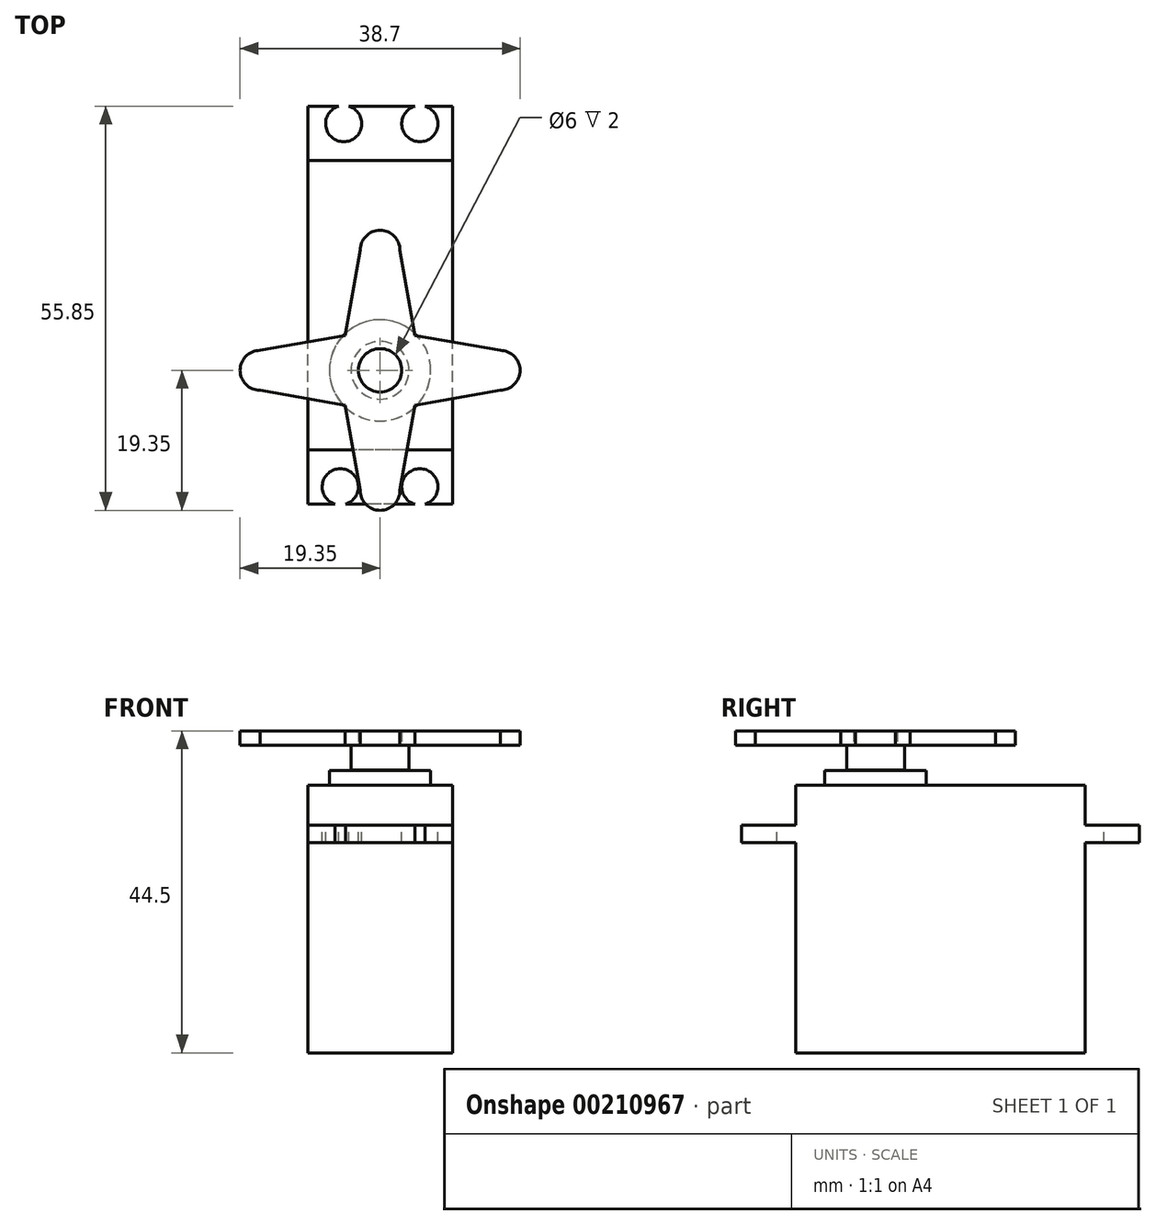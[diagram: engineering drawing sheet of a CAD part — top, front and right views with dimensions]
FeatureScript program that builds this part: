
annotation { "Feature Type Name" : "Feature", "Feature Type Description" : "" }
export const myFeature = defineFeature(function(context is Context, id is Id, definition is map)
    precondition{}
    {
        {
            var Q0;
            Q0=qCreatedBy(makeId("Top.planeOp"),FACE);
            var sketch = newSketch(context, id + "F0", { "sketchPlane" : qUnion([Q0])});
            skLineSegment(sketch, "E0.bottom", {"start": v(10, -18.5) * mm, "end": v(-10, -18.5) * mm});
            skLineSegment(sketch, "E0.top", {"start": v(10, 36.5) * mm, "end": v(-10, 36.5) * mm});
            skLineSegment(sketch, "E0.left", {"start": v(10, -18.5) * mm, "end": v(10, 36.5) * mm});
            skLineSegment(sketch, "E0.right", {"start": v(-10, -18.5) * mm, "end": v(-10, 36.5) * mm});
            skPoint(sketch, "E0.middle", {"position": v(0, 9) * mm});
            skLineSegment(sketch, "E1.bottom", {"start": v(10, -11) * mm, "end": v(-10, -11) * mm});
            skLineSegment(sketch, "E1.top", {"start": v(10, 29) * mm, "end": v(-10, 29) * mm});
            skLineSegment(sketch, "E1.left", {"start": v(10, -11) * mm, "end": v(10, 29) * mm});
            skLineSegment(sketch, "E1.right", {"start": v(-10, -11) * mm, "end": v(-10, 29) * mm});
            skCircle(sketch, "E2", {"center": v(0, 0) * mm, "radius": 7 * mm});
            skCircle(sketch, "E3", {"center": v(0, 0) * mm, "radius": 3 * mm});
            skCircle(sketch, "E4", {"center": v(-5.5, -16.1) * mm, "radius": 2.5 * mm});
            skCircle(sketch, "E5.MirrorC", {"center": v(5.5, -16.1) * mm, "radius": 2.5 * mm});
            skCircle(sketch, "E6.MirrorC", {"center": v(5.5, 34.1) * mm, "radius": 2.5 * mm});
            skCircle(sketch, "E7.MirrorC", {"center": v(-5.03, 34.1) * mm, "radius": 2.5 * mm});
            skSolve(sketch);
        }
        {
            var Q0;
            Q0=makeQuery(id+"F0.imprint","IMPRINT",FACE,{"disambiguationData":[TD([[makeQuery(id+"F0.imprint","IMPRINT",EDGE,{"derivedFrom":sQuery(id+"F0.wireOp",EDGE,"E2")}),1.0]])]});
            var Q1;
            Q1=makeQuery(id+"F0.imprint","IMPRINT",FACE,{"disambiguationData":[TD([[makeQuery(id+"F0.imprint","IMPRINT",EDGE,{"derivedFrom":sQuery(id+"F0.wireOp",EDGE,"E3")}),1.0]])]});
            extrude(context, id + "F1", {"entities" : qUnion([Q0, Q1]), "depth" : 2 * mm});
        }
        {
            var Q0;
            Q0=makeQuery(id+"F0.imprint","IMPRINT",FACE,{"disambiguationData":[TD([[makeQuery(id+"F0.imprint","IMPRINT",EDGE,{"derivedFrom":sQuery(id+"F0.wireOp",EDGE,"E3")}),1.0]])]});
            var Q1;
            Q1=sQuery(id+"F0.wireOp",EDGE,"E3");
            extrude(context, id + "F2", {"entities" : qUnion([Q0]), "operationType" : NewBodyOperationType.ADD, "surfaceEntities" : qUnion([Q1]), "depth" : 5.5 * mm});
        }
        {
            var Q0;
            Q0=makeQuery(id+"F0.imprint","IMPRINT",FACE,{"disambiguationData":[TD([[makeQuery(id+"F0.imprint","IMPRINT",EDGE,{"derivedFrom":sQuery(id+"F0.wireOp",EDGE,"E1.bottom")}),-1.0]])]});
            var Q1;
            Q1=makeQuery(id+"F0.imprint","IMPRINT",FACE,{"disambiguationData":[TD([[makeQuery(id+"F0.imprint","IMPRINT",EDGE,{"derivedFrom":sQuery(id+"F0.wireOp",EDGE,"E2")}),1.0]])]});
            var Q2;
            Q2=makeQuery(id+"F0.imprint","IMPRINT",FACE,{"disambiguationData":[TD([[makeQuery(id+"F0.imprint","IMPRINT",EDGE,{"derivedFrom":sQuery(id+"F0.wireOp",EDGE,"E3")}),1.0]])]});
            extrude(context, id + "F3", {"entities" : qUnion([Q0, Q1, Q2]), "operationType" : NewBodyOperationType.ADD, "oppositeDirection" : true, "depth" : 37 * mm});
        }
        {
            var Q0;
            {var subQ2=sQuery(id+"F0.wireOp",EDGE,"E0.top");Q0=makeQuery(id+"F0.imprint","IMPRINT",FACE,{"disambiguationData":[TD([[makeQuery(id+"F0.imprint","IMPRINT",EDGE,{"derivedFrom":subQ2}),1.0]])]});}
            var Q1;
            {var subQ2=sQuery(id+"F0.wireOp",EDGE,"E0.bottom");Q1=makeQuery(id+"F0.imprint","IMPRINT",FACE,{"disambiguationData":[TD([[makeQuery(id+"F0.imprint","IMPRINT",EDGE,{"derivedFrom":subQ2}),-1.0]])]});}
            extrude(context, id + "F4", {"entities" : qUnion([Q0, Q1]), "operationType" : NewBodyOperationType.ADD, "oppositeDirection" : true, "depth" : 7.95 * mm, "hasSecondDirection" : true, "secondDirectionOppositeDirection" : true, "secondDirectionDepth" : 5.5 * mm});
        }
        {
            var Q0;
            Q0=makeQuery(id+"F2.opExtrude","CAP_FACE",FACE,{"disambiguationData":[OSD([sQuery(id+"F0.wireOp",EDGE,"E3")])],"isStart":false});
            var sketch = newSketch(context, id + "F5", { "sketchPlane" : qUnion([Q0])});
            skCircle(sketch, "E8.0", {"center": v(0, 0) * mm, "radius": 3 * mm});
            skCircle(sketch, "E9", {"center": v(0, 0) * mm, "radius": 4 * mm});
            skLineSegment(sketch, "E10.left", {"start": v(19.35, 0) * mm, "end": v(19.35, 0) * mm});
            skLineSegment(sketch, "E10.right", {"start": v(-19.35, 0) * mm, "end": v(-19.35, 0) * mm});
            skLineSegment(sketch, "E11.bottom", {"start": v(0, -19.35) * mm, "end": v(0, -19.35) * mm});
            skLineSegment(sketch, "E11.top", {"start": v(0, 19.35) * mm, "end": v(0, 19.35) * mm});
            skPoint(sketch, "E12.visualSharp", {"position": v(-19.35, -2.75) * mm});
            skArc(sketch, "E12.filletArc", {"start": v(-19.35, 0) * mm, "mid": v(-18.54, -1.94) * mm, "end": v(-16.6, -2.75) * mm});
            skPoint(sketch, "E13.visualSharp", {"position": v(-19.35, 2.75) * mm});
            skArc(sketch, "E13.filletArc", {"start": v(-16.6, 2.75) * mm, "mid": v(-18.54, 1.94) * mm, "end": v(-19.35, 0) * mm});
            skPoint(sketch, "E14.visualSharp", {"position": v(-2.75, 19.35) * mm});
            skArc(sketch, "E14.filletArc", {"start": v(0, 19.35) * mm, "mid": v(-1.94, 18.54) * mm, "end": v(-2.75, 16.6) * mm});
            skPoint(sketch, "E15.visualSharp", {"position": v(2.75, 19.35) * mm});
            skArc(sketch, "E15.filletArc", {"start": v(2.75, 16.6) * mm, "mid": v(1.94, 18.54) * mm, "end": v(0, 19.35) * mm});
            skPoint(sketch, "E16.visualSharp", {"position": v(19.35, 2.75) * mm});
            skArc(sketch, "E16.filletArc", {"start": v(19.35, 0) * mm, "mid": v(18.54, 1.94) * mm, "end": v(16.6, 2.75) * mm});
            skPoint(sketch, "E17.visualSharp", {"position": v(19.35, -2.75) * mm});
            skArc(sketch, "E17.filletArc", {"start": v(16.6, -2.75) * mm, "mid": v(18.54, -1.94) * mm, "end": v(19.35, 0) * mm});
            skPoint(sketch, "E18.visualSharp", {"position": v(-2.75, -19.35) * mm});
            skArc(sketch, "E18.filletArc", {"start": v(-2.75, -16.6) * mm, "mid": v(-1.94, -18.54) * mm, "end": v(0, -19.35) * mm});
            skPoint(sketch, "E19.visualSharp", {"position": v(2.75, -19.35) * mm});
            skArc(sketch, "E19.filletArc", {"start": v(0, -19.35) * mm, "mid": v(1.94, -18.54) * mm, "end": v(2.75, -16.6) * mm});
            skLineSegment(sketch, "E20", {"start": v(2.75, 16.6) * mm, "end": v(4.8, 4.8) * mm});
            skLineSegment(sketch, "E21", {"start": v(4.8, 4.8) * mm, "end": v(16.6, 2.75) * mm});
            skLineSegment(sketch, "E22", {"start": v(-2.75, 16.6) * mm, "end": v(-4.8, 4.8) * mm});
            skLineSegment(sketch, "E23", {"start": v(-4.8, 4.8) * mm, "end": v(-16.6, 2.75) * mm});
            skLineSegment(sketch, "E24", {"start": v(-16.6, -2.75) * mm, "end": v(-4.8, -4.8) * mm});
            skLineSegment(sketch, "E25", {"start": v(-4.8, -4.8) * mm, "end": v(-2.75, -16.6) * mm});
            skLineSegment(sketch, "E26", {"start": v(2.75, -16.6) * mm, "end": v(4.8, -4.8) * mm});
            skLineSegment(sketch, "E27", {"start": v(4.8, -4.8) * mm, "end": v(16.6, -2.75) * mm});
            skSolve(sketch);
        }
        {
            var Q0;
            Q0=makeQuery(id+"F5.imprint","IMPRINT",FACE,{"disambiguationData":[TD([[makeQuery(id+"F5.imprint","IMPRINT",EDGE,{"derivedFrom":sQuery(id+"F5.wireOp",EDGE,"E9")}),-1.0]])]});
            var Q1;
            Q1=makeQuery(id+"F5.imprint","IMPRINT",FACE,{"disambiguationData":[TD([[makeQuery(id+"F5.imprint","IMPRINT",EDGE,{"derivedFrom":sQuery(id+"F5.wireOp",EDGE,"E8.0")}),-1.0]])]});
            extrude(context, id + "F6", {"entities" : qUnion([Q0, Q1]), "depth" : 2 * mm});
        }
        {
            var Q0;
            Q0=makeQuery(id+"F5.imprint","IMPRINT",FACE,{"disambiguationData":[TD([[makeQuery(id+"F5.imprint","IMPRINT",EDGE,{"derivedFrom":sQuery(id+"F5.wireOp",EDGE,"E8.0")}),-1.0]])]});
            extrude(context, id + "F7", {"entities" : qUnion([Q0]), "operationType" : NewBodyOperationType.ADD, "oppositeDirection" : true, "depth" : 3.4 * mm});
        }
    });
